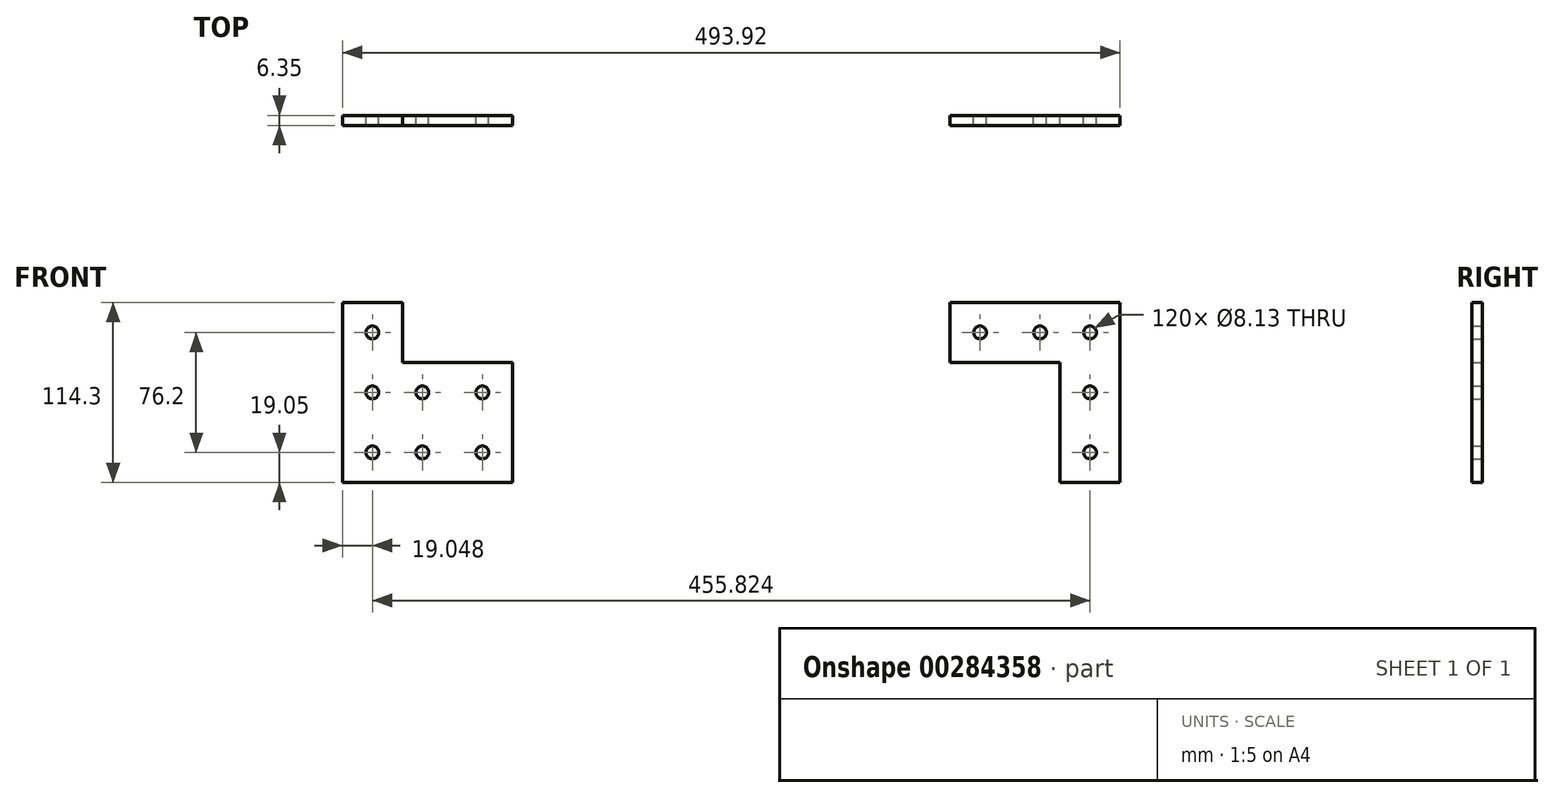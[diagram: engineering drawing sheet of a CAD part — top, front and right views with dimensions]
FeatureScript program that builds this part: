
annotation { "Feature Type Name" : "Feature", "Feature Type Description" : "" }
export const myFeature = defineFeature(function(context is Context, id is Id, definition is map)
    precondition{}
    {
        {
            var Q0;
            Q0=qCreatedBy(makeId("Front.planeOp"),FACE);
            var sketch = newSketch(context, id + "F0", { "sketchPlane" : qUnion([Q0])});
            skArc(sketch, "E0", {"start": v(-225.88, 34.58) * mm, "mid": v(-224.4, 36.07) * mm, "end": v(-223.85, 38.1) * mm});
            skArc(sketch, "E1", {"start": v(-223.85, 38.1) * mm, "mid": v(-227.91, 42.16) * mm, "end": v(-231.98, 38.1) * mm});
            skArc(sketch, "E2", {"start": v(-231.98, 38.1) * mm, "mid": v(-229.94, 34.58) * mm, "end": v(-225.88, 34.58) * mm});
            skArc(sketch, "E3", {"start": v(-200.23, 0) * mm, "mid": v(-196.16, -4.06) * mm, "end": v(-192.1, 0) * mm});
            skArc(sketch, "E4", {"start": v(-192.1, 0) * mm, "mid": v(-196.16, 4.06) * mm, "end": v(-200.23, 0) * mm});
            skArc(sketch, "E5", {"start": v(-228.7, -3.99) * mm, "mid": v(-225.33, -3.14) * mm, "end": v(-223.85, 0) * mm});
            skArc(sketch, "E6", {"start": v(-223.85, 0) * mm, "mid": v(-227.91, 4.06) * mm, "end": v(-231.98, 0) * mm});
            skArc(sketch, "E7", {"start": v(-231.98, 0) * mm, "mid": v(-231.05, -2.58) * mm, "end": v(-228.7, -3.99) * mm});
            skArc(sketch, "E8", {"start": v(-223.88, -38.63) * mm, "mid": v(-223.86, -38.37) * mm, "end": v(-223.85, -38.1) * mm});
            skArc(sketch, "E9", {"start": v(-223.85, -38.1) * mm, "mid": v(-227.91, -34.04) * mm, "end": v(-231.98, -38.1) * mm});
            skArc(sketch, "E10", {"start": v(-231.98, -38.1) * mm, "mid": v(-228.18, -42.16) * mm, "end": v(-223.88, -38.63) * mm});
            skArc(sketch, "E11", {"start": v(-192.1, -38.1) * mm, "mid": v(-196.16, -34.04) * mm, "end": v(-200.23, -38.1) * mm});
            skArc(sketch, "E12", {"start": v(-200.23, -38.1) * mm, "mid": v(-196.16, -42.16) * mm, "end": v(-192.1, -38.1) * mm});
            skArc(sketch, "E13", {"start": v(-157.93, -34.04) * mm, "mid": v(-160.89, -35.18) * mm, "end": v(-162.13, -38.1) * mm});
            skArc(sketch, "E14", {"start": v(-162.13, -38.1) * mm, "mid": v(-158.06, -42.16) * mm, "end": v(-154, -38.1) * mm});
            skArc(sketch, "E15", {"start": v(-154, -38.1) * mm, "mid": v(-155.14, -35.27) * mm, "end": v(-157.93, -34.04) * mm});
            skArc(sketch, "E16", {"start": v(-157.01, -3.93) * mm, "mid": v(-154.14, -1.05) * mm, "end": v(-155.19, 2.87) * mm});
            skArc(sketch, "E17", {"start": v(-155.19, 2.87) * mm, "mid": v(-159.62, 3.75) * mm, "end": v(-162.13, 0) * mm});
            skArc(sketch, "E18", {"start": v(-162.13, 0) * mm, "mid": v(-160.54, -3.22) * mm, "end": v(-157.01, -3.93) * mm});
            skLineSegment(sketch, "E19", {"start": v(-139.01, -57.15) * mm, "end": v(-246.96, -57.15) * mm});
            skLineSegment(sketch, "E20", {"start": v(-246.96, -57.15) * mm, "end": v(-246.96, 57.15) * mm});
            skLineSegment(sketch, "E21", {"start": v(-246.96, 57.15) * mm, "end": v(-208.86, 57.15) * mm});
            skLineSegment(sketch, "E22", {"start": v(-208.86, 57.15) * mm, "end": v(-208.86, 19.05) * mm});
            skLineSegment(sketch, "E23", {"start": v(-208.86, 19.05) * mm, "end": v(-139.01, 19.05) * mm});
            skLineSegment(sketch, "E24", {"start": v(-139.01, 19.05) * mm, "end": v(-139.01, -57.15) * mm});
            skArc(sketch, "E25", {"start": v(225.88, -34.58) * mm, "mid": v(224.4, -36.07) * mm, "end": v(223.85, -38.1) * mm});
            skArc(sketch, "E26", {"start": v(223.85, -38.1) * mm, "mid": v(227.91, -42.16) * mm, "end": v(231.98, -38.1) * mm});
            skArc(sketch, "E27", {"start": v(231.98, -38.1) * mm, "mid": v(229.94, -34.58) * mm, "end": v(225.88, -34.58) * mm});
            skArc(sketch, "E28", {"start": v(162.05, 37.3) * mm, "mid": v(162.1, 37.7) * mm, "end": v(162.13, 38.1) * mm});
            skArc(sketch, "E29", {"start": v(162.13, 38.1) * mm, "mid": v(158.06, 42.16) * mm, "end": v(154, 38.1) * mm});
            skArc(sketch, "E30", {"start": v(154, 38.1) * mm, "mid": v(157.66, 34.06) * mm, "end": v(162.05, 37.3) * mm});
            skArc(sketch, "E31", {"start": v(200.23, 38.1) * mm, "mid": v(196.16, 42.16) * mm, "end": v(192.1, 38.1) * mm});
            skArc(sketch, "E32", {"start": v(192.1, 38.1) * mm, "mid": v(196.16, 34.04) * mm, "end": v(200.23, 38.1) * mm});
            skArc(sketch, "E33", {"start": v(227.91, 34.04) * mm, "mid": v(230.79, 35.23) * mm, "end": v(231.98, 38.1) * mm});
            skArc(sketch, "E34", {"start": v(231.98, 38.1) * mm, "mid": v(228.44, 42.13) * mm, "end": v(223.99, 39.15) * mm});
            skArc(sketch, "E35", {"start": v(223.99, 39.15) * mm, "mid": v(224.69, 35.63) * mm, "end": v(227.91, 34.04) * mm});
            skArc(sketch, "E36", {"start": v(223.93, 0.8) * mm, "mid": v(223.87, 0.4) * mm, "end": v(223.85, 0) * mm});
            skArc(sketch, "E37", {"start": v(223.85, 0) * mm, "mid": v(227.91, -4.06) * mm, "end": v(231.98, 0) * mm});
            skArc(sketch, "E38", {"start": v(231.98, 0) * mm, "mid": v(228.31, 4.04) * mm, "end": v(223.93, 0.8) * mm});
            skLineSegment(sketch, "E39", {"start": v(139.01, 57.15) * mm, "end": v(246.96, 57.15) * mm});
            skLineSegment(sketch, "E40", {"start": v(246.96, 57.15) * mm, "end": v(246.96, -57.15) * mm});
            skLineSegment(sketch, "E41", {"start": v(246.96, -57.15) * mm, "end": v(208.86, -57.15) * mm});
            skLineSegment(sketch, "E42", {"start": v(208.86, -57.15) * mm, "end": v(208.86, 19.05) * mm});
            skLineSegment(sketch, "E43", {"start": v(139.01, 57.15) * mm, "end": v(139.01, 19.05) * mm});
            skLineSegment(sketch, "E44", {"start": v(139.01, 19.05) * mm, "end": v(208.86, 19.05) * mm});
            skSolve(sketch);
        }
        {
            var Q0;
            Q0=qSketchRegion(id+"F0",true);
            extrude(context, id + "F1", {"entities" : qUnion([Q0]), "depth" : 6.35 * mm});
        }
    });
